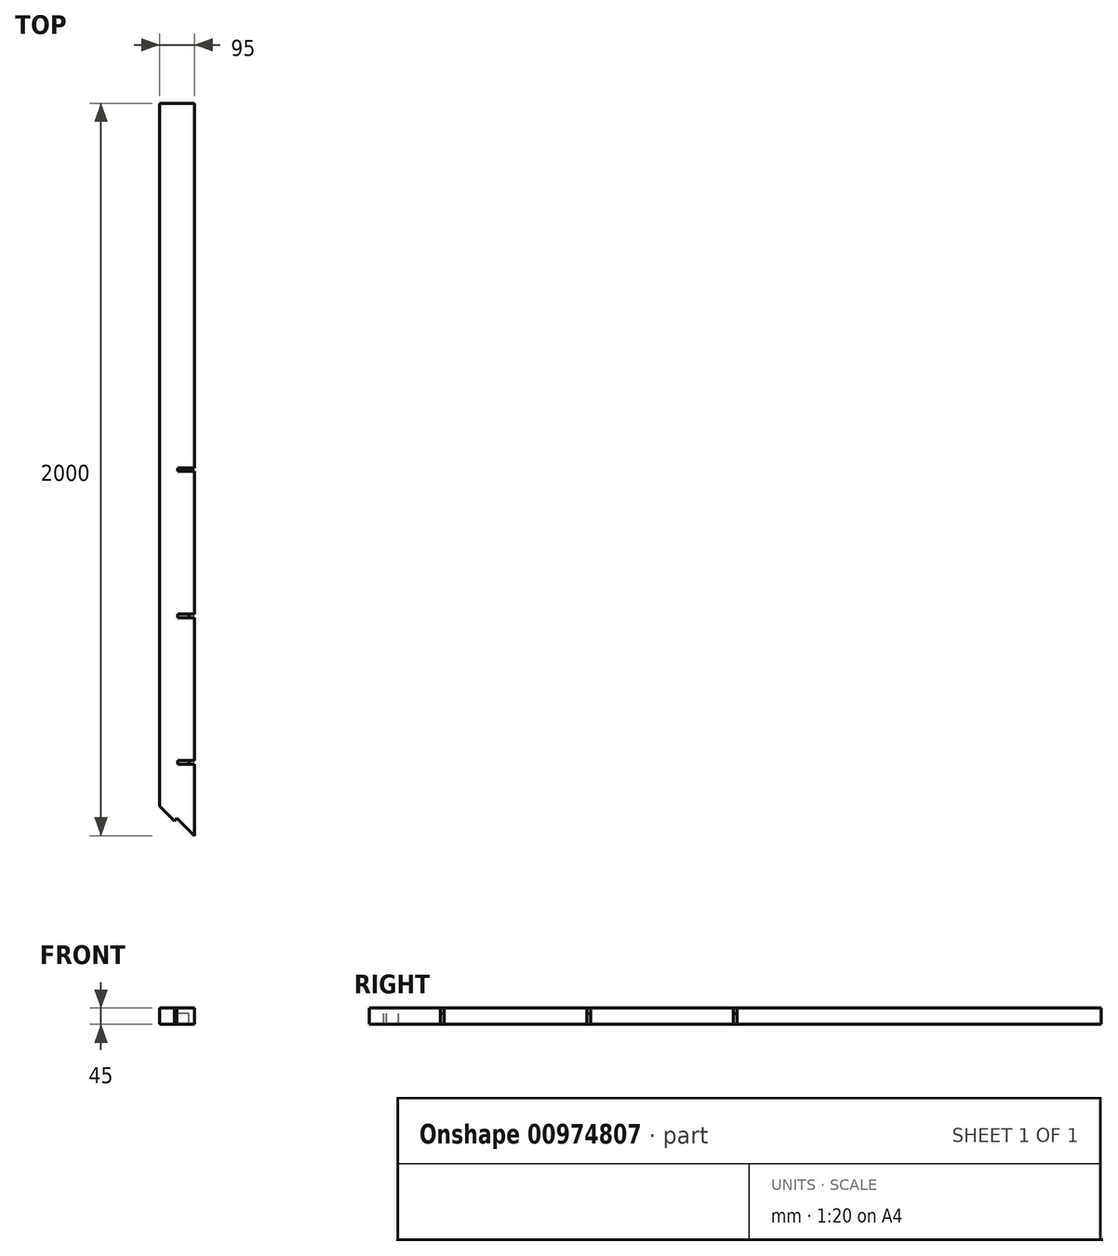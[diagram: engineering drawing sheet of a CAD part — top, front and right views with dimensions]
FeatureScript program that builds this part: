
annotation { "Feature Type Name" : "Feature", "Feature Type Description" : "" }
export const myFeature = defineFeature(function(context is Context, id is Id, definition is map)
    precondition{}
    {
        {
            var Q0;
            Q0=qCreatedBy(makeId("Front.planeOp"),FACE);
            var sketch = newSketch(context, id + "F0", { "sketchPlane" : qUnion([Q0])});
            skLineSegment(sketch, "E0.bottom", {"start": v(-47.5, -22.5) * mm, "end": v(47.5, -22.5) * mm});
            skLineSegment(sketch, "E0.top", {"start": v(-47.5, 22.5) * mm, "end": v(47.5, 22.5) * mm});
            skLineSegment(sketch, "E0.left", {"start": v(-47.5, -22.5) * mm, "end": v(-47.5, 22.5) * mm});
            skLineSegment(sketch, "E0.right", {"start": v(47.5, -22.5) * mm, "end": v(47.5, 22.5) * mm});
            skPoint(sketch, "E0.middle", {"position": v(0, 0) * mm});
            skSolve(sketch);
        }
        {
            var Q0;
            Q0 = qSketchRegion(id + "F0", true);
            extrude(context, id + "F1", {"entities" : qUnion([Q0]), "endBound" : BoundingType.SYMMETRIC, "depth" : 2500 * mm, "offsetDistance" : 25 * mm});
        }
        {
            var Q0;
            Q0=makeQuery(id+"F1.opExtrude","SWEPT_FACE",FACE,{"disambiguationData":[OSD([sQuery(id+"F0.wireOp",EDGE,"E0.top")])]});
            var sketch = newSketch(context, id + "F2", { "sketchPlane" : qUnion([Q0])});
            skLineSegment(sketch, "E1", {"start": v(-47.5, 1000) * mm, "end": v(47.5, 1000) * mm});
            skLineSegment(sketch, "E2", {"start": v(47.5, 1000) * mm, "end": v(47.5, 1250) * mm});
            skLineSegment(sketch, "E3", {"start": v(47.5, 1250) * mm, "end": v(-47.5, 1250) * mm});
            skLineSegment(sketch, "E4", {"start": v(-47.5, 1250) * mm, "end": v(-47.5, 1000) * mm});
            skLineSegment(sketch, "E5", {"start": v(47.5, -1000) * mm, "end": v(47.5, -1250) * mm});
            skLineSegment(sketch, "E6", {"start": v(47.5, -1250) * mm, "end": v(-47.5, -1250) * mm});
            skLineSegment(sketch, "E7", {"start": v(-47.5, -1250) * mm, "end": v(-47.5, -905) * mm});
            skLineSegment(sketch, "E8", {"start": v(-47.5, -905) * mm, "end": v(47.5, -1000) * mm});
            skSolve(sketch);
        }
        {
            var Q0;
            Q0 = qSketchRegion(id + "F2", true);
            extrude(context, id + "F3", {"entities" : qUnion([Q0]), "operationType" : NewBodyOperationType.REMOVE, "endBound" : BoundingType.UP_TO_NEXT, "oppositeDirection" : true, "depth" : 25 * mm, "offsetDistance" : 25 * mm});
        }
        {
            var Q0;
            Q0=qCreatedBy(makeId("Front.planeOp"),FACE);
            var sketch = newSketch(context, id + "F4", { "sketchPlane" : qUnion([Q0])});
            skLineSegment(sketch, "E9", {"start": v(2.5, 22.5) * mm, "end": v(47.5, 22.5) * mm});
            skLineSegment(sketch, "E10", {"start": v(47.5, 22.5) * mm, "end": v(47.5, -22.5) * mm});
            skLineSegment(sketch, "E11", {"start": v(47.5, -22.5) * mm, "end": v(32.5, -22.5) * mm});
            skLineSegment(sketch, "E12", {"start": v(32.5, -22.5) * mm, "end": v(32.5, 7.5) * mm});
            skLineSegment(sketch, "E13", {"start": v(32.5, 7.5) * mm, "end": v(2.5, 7.5) * mm});
            skLineSegment(sketch, "E14", {"start": v(2.5, 7.5) * mm, "end": v(2.5, 22.5) * mm});
            skSolve(sketch);
        }
        {
            var Q0;
            Q0 = qSketchRegion(id + "F4", true);
            extrude(context, id + "F5", {"entities" : qUnion([Q0]), "operationType" : NewBodyOperationType.REMOVE, "endBound" : BoundingType.SYMMETRIC, "oppositeDirection" : true, "depth" : 10 * mm, "offsetDistance" : 25 * mm});
        }
        {
            var Q0;
            Q0=qCreatedBy(makeId("Front.planeOp"),FACE);
            cPlane(context, id + "F6", {"entities" : qUnion([Q0]), "cplaneType" : CPlaneType.OFFSET, "offset" : 800 * mm, "width" : 150 * mm, "height" : 150 * mm});
        }
        {
            var Q0;
            Q0=qCreatedBy(id+"F6.planeOp",FACE);
            var sketch = newSketch(context, id + "F7", { "sketchPlane" : qUnion([Q0])});
            skLineSegment(sketch, "E15.0", {"start": v(2.5, 7.5) * mm, "end": v(2.5, 22.5) * mm});
            skLineSegment(sketch, "E16.0", {"start": v(2.5, 22.5) * mm, "end": v(47.5, 22.5) * mm});
            skLineSegment(sketch, "E17.0", {"start": v(47.5, 22.5) * mm, "end": v(47.5, -22.5) * mm});
            skLineSegment(sketch, "E18.0", {"start": v(47.5, -22.5) * mm, "end": v(32.5, -22.5) * mm});
            skLineSegment(sketch, "E19.0", {"start": v(32.5, -22.5) * mm, "end": v(32.5, 7.5) * mm});
            skLineSegment(sketch, "E20.0", {"start": v(32.5, 7.5) * mm, "end": v(2.5, 7.5) * mm});
            skSolve(sketch);
        }
        {
            var Q0;
            Q0 = qSketchRegion(id + "F7", true);
            extrude(context, id + "F8", {"entities" : qUnion([Q0]), "operationType" : NewBodyOperationType.REMOVE, "endBound" : BoundingType.SYMMETRIC, "oppositeDirection" : true, "depth" : 10 * mm, "offsetDistance" : 25 * mm});
        }
        {
            var Q0;
            Q0=qCreatedBy(makeId("Front.planeOp"),FACE);
            cPlane(context, id + "F9", {"entities" : qUnion([Q0]), "cplaneType" : CPlaneType.OFFSET, "offset" : 400 * mm, "width" : 150 * mm, "height" : 150 * mm});
        }
        {
            var Q0;
            Q0=qCreatedBy(id+"F9.planeOp",FACE);
            var sketch = newSketch(context, id + "F10", { "sketchPlane" : qUnion([Q0])});
            skLineSegment(sketch, "E21.0", {"start": v(2.5, 7.5) * mm, "end": v(2.5, 22.5) * mm});
            skLineSegment(sketch, "E22.0", {"start": v(32.5, 7.5) * mm, "end": v(2.5, 7.5) * mm});
            skLineSegment(sketch, "E23.0", {"start": v(32.5, -22.5) * mm, "end": v(32.5, 7.5) * mm});
            skLineSegment(sketch, "E24.0", {"start": v(47.5, -22.5) * mm, "end": v(32.5, -22.5) * mm});
            skLineSegment(sketch, "E25.0", {"start": v(47.5, 22.5) * mm, "end": v(47.5, -22.5) * mm});
            skLineSegment(sketch, "E26.0", {"start": v(2.5, 22.5) * mm, "end": v(47.5, 22.5) * mm});
            skSolve(sketch);
        }
        {
            var Q0;
            Q0 = qSketchRegion(id + "F10", true);
            extrude(context, id + "F11", {"entities" : qUnion([Q0]), "operationType" : NewBodyOperationType.REMOVE, "endBound" : BoundingType.SYMMETRIC, "depth" : 10 * mm, "offsetDistance" : 25 * mm});
        }
        {
            var Q0;
            Q0=makeQuery(id+"F1.opExtrude","SWEPT_FACE",FACE,{"disambiguationData":[OSD([sQuery(id+"F0.wireOp",EDGE,"E0.top")])]});
            var sketch = newSketch(context, id + "F12", { "sketchPlane" : qUnion([Q0])});
            skLineSegment(sketch, "E27", {"start": v(-47.5, -905) * mm, "end": v(0, -952.5) * mm});
            skLineSegment(sketch, "E28", {"start": v(0, -952.5) * mm, "end": v(-7.07, -959.57) * mm});
            skLineSegment(sketch, "E29", {"start": v(-7.07, -959.57) * mm, "end": v(-47.5, -919.14) * mm});
            skLineSegment(sketch, "E30", {"start": v(-47.5, -919.14) * mm, "end": v(-47.5, -905) * mm});
            skSolve(sketch);
        }
        {
            var Q0;
            Q0 = qSketchRegion(id + "F12", true);
            var Q1;
            Q1=makeQuery(id+"F1.opExtrude","SWEPT_FACE",FACE,{"disambiguationData":[OSD([sQuery(id+"F0.wireOp",EDGE,"E0.bottom")])]});
            extrude(context, id + "F13", {"entities" : qUnion([Q0]), "operationType" : NewBodyOperationType.ADD, "endBound" : BoundingType.UP_TO_SURFACE, "oppositeDirection" : true, "depth" : 25 * mm, "endBoundEntityFace" : qUnion([Q1]), "offsetDistance" : 25 * mm});
        }
    });
